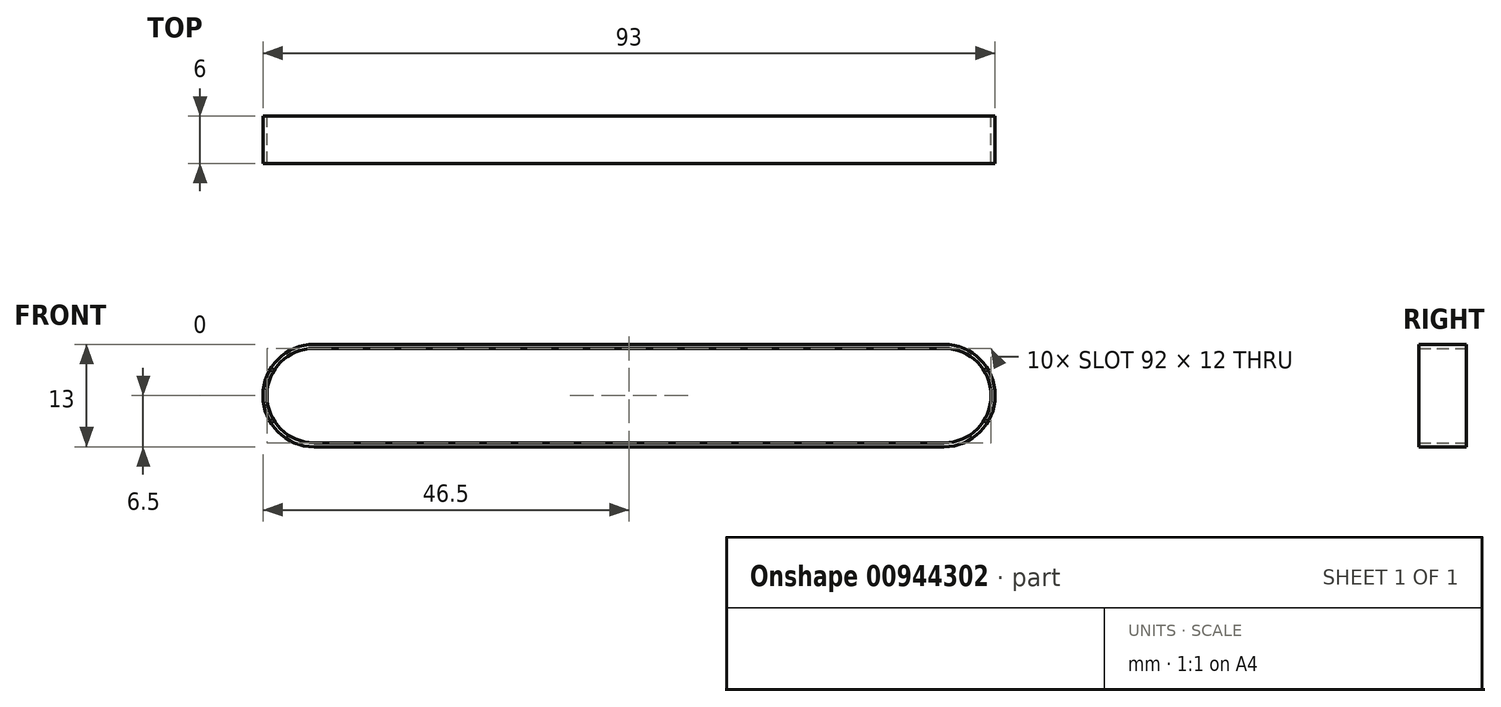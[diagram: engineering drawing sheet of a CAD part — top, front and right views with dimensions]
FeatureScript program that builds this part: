
annotation { "Feature Type Name" : "Feature", "Feature Type Description" : "" }
export const myFeature = defineFeature(function(context is Context, id is Id, definition is map)
    precondition{}
    {
        {
            var Q0;
            Q0=qCreatedBy(makeId("Front.planeOp"),FACE);
            var sketch = newSketch(context, id + "F0", { "sketchPlane" : qUnion([Q0])});
            skLineSegment(sketch, "E0", {"start": v(100.06, 0) * mm, "end": v(238.5, 0) * mm, "construction": true});
            skArc(sketch, "E1", {"start": v(-40, 6.5) * mm, "mid": v(-46.5, 0) * mm, "end": v(-40, -6.5) * mm});
            skLineSegment(sketch, "E2", {"start": v(-40, 6.5) * mm, "end": v(0, 6.5) * mm});
            skLineSegment(sketch, "E3", {"start": v(-40, -6.5) * mm, "end": v(0, -6.5) * mm});
            skArc(sketch, "E4", {"start": v(-40, 6) * mm, "mid": v(-46, 0) * mm, "end": v(-40, -6) * mm});
            skLineSegment(sketch, "E5", {"start": v(-40, -6) * mm, "end": v(0, -6) * mm});
            skLineSegment(sketch, "E6.MirrorCS", {"start": v(69.44, 0) * mm, "end": v(-69, 0) * mm, "construction": true});
            skLineSegment(sketch, "E7", {"start": v(0, 0) * mm, "end": v(0, 27.23) * mm, "construction": true});
            skLineSegment(sketch, "E8", {"start": v(-40, 6) * mm, "end": v(0, 6) * mm});
            skLineSegment(sketch, "E9", {"start": v(0, 6) * mm, "end": v(-0.22, 5.14) * mm});
            skLineSegment(sketch, "E10.MirrorCS", {"start": v(40, 6) * mm, "end": v(0, 6) * mm});
            skLineSegment(sketch, "E11.MirrorCS", {"start": v(40, 6.5) * mm, "end": v(0, 6.5) * mm});
            skArc(sketch, "E12.MirrorCS", {"start": v(40, 6) * mm, "mid": v(46, 0) * mm, "end": v(40, -6) * mm});
            skArc(sketch, "E13.MirrorCS", {"start": v(40, 6.5) * mm, "mid": v(46.5, 0) * mm, "end": v(40, -6.5) * mm});
            skLineSegment(sketch, "E14.MirrorCS", {"start": v(40, -6) * mm, "end": v(0, -6) * mm});
            skLineSegment(sketch, "E15.MirrorCS", {"start": v(40, -6.5) * mm, "end": v(0, -6.5) * mm});
            skSolve(sketch);
        }
        {
            var Q0;
            Q0=qSketchRegion(id+"F0",true);
            extrude(context, id + "F1", {"entities" : qUnion([Q0]), "depth" : 6 * mm, "offsetDistance" : 25 * mm});
        }
    });
